# Revit family: QF_ADVENTYS_ADV1662-A_KNL16_32000_Front_to_Back
name_source: partatom
category: Attrezzature speciali
units: mm (PartAtom-declared; Revit-internal decimal feet)

## family parameters
Condiviso = No
Host = Superficie
Punto di calcolo locali = No
Quota connettore circolare = Usa diametro
Taglio con vuoti quando caricato = No
Tipo di parte = Normale

## types (1)
- ADV1662-A
    CW2 = 210 mm  [stored 0.688976 ft]
    Controller_Height = 120 mm  [stored 0.393701 ft]
    Controller_Width = 420 mm  [stored 1.37795 ft]
    Cycle = 50 Hz
    Depth = 690 mm  [stored 2.26378 ft]
    Depth Actual = 690 mm  [stored 2.26378 ft]
    Height = 66.5 mm  [stored 0.218176 ft]
    Height Actual = 66.5 mm  [stored 0.218176 ft]
    Height_Generator = 98.5 mm
    Item Number = ADV1662-A
    Length Actual = 690 mm  [stored 2.26378 ft]
    Modello = KNL16 32000 Front to Back
    Phase = 3
    Produttore = ADVENTYS
    Prospetto di default = 1219.2 mm  [stored 4 ft]
    URL = https://adventys.com
    Volts = 380 V
    Watts = 32000 W
    Weight = 75
    Width = 690 mm  [stored 2.26378 ft]
    Width_Generator = 294 mm  [stored 0.964567 ft]

note: [stored X ft] marks values corroborated as IEEE doubles in the binary element streams (Revit-internal decimal feet)

## geometry (parser evidence)
native form markers: Blend x2, Sweep x1
no freeform markers — native parametric forms only
